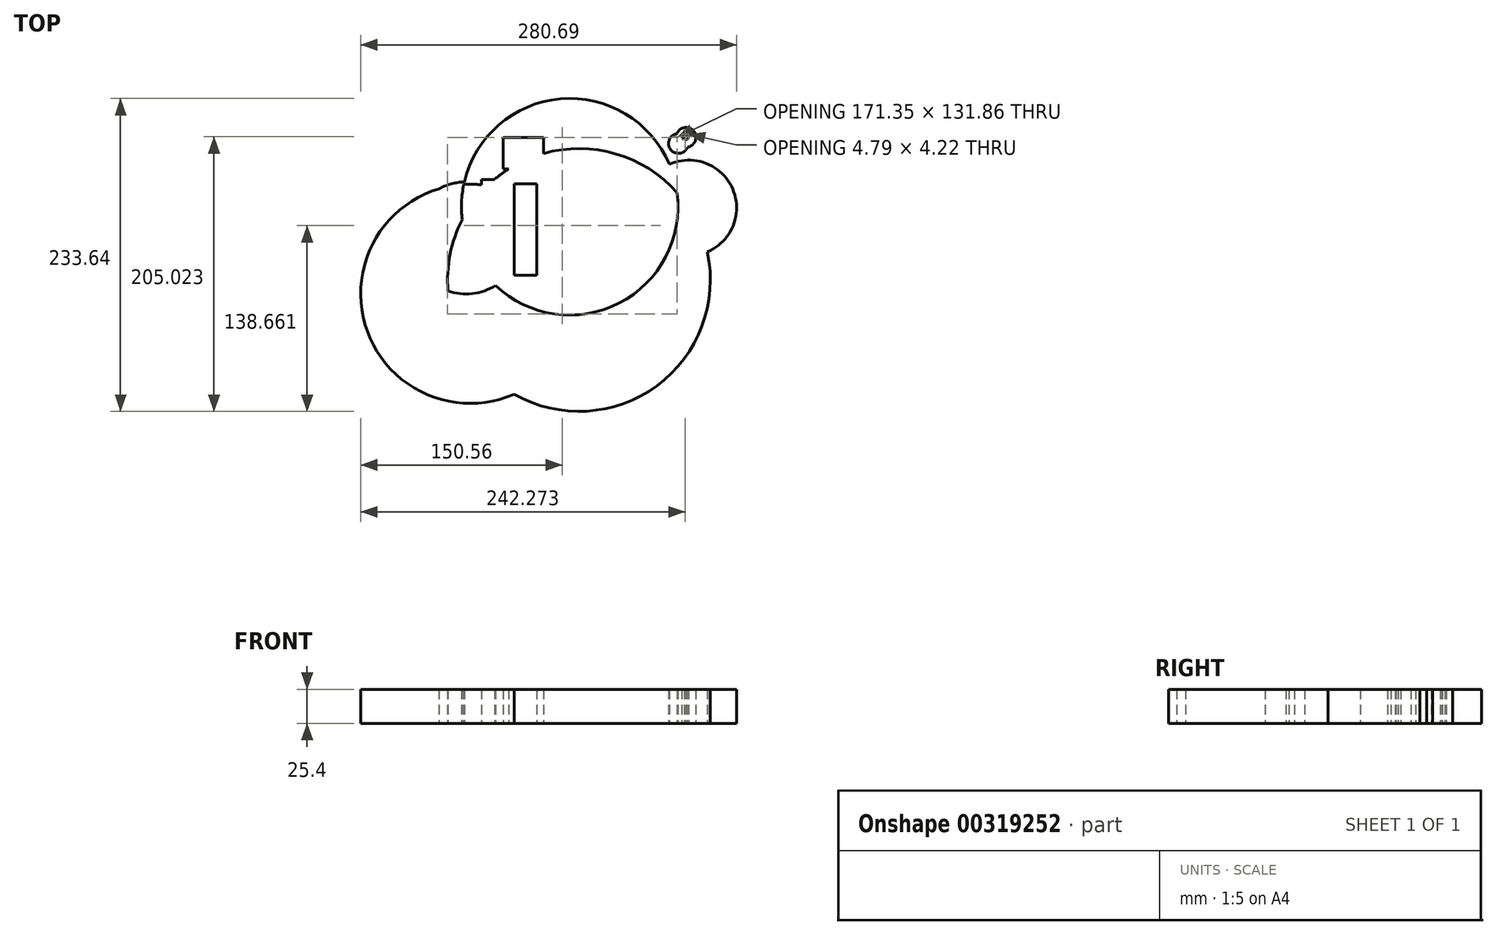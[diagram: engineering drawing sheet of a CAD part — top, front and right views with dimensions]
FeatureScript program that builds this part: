
annotation { "Feature Type Name" : "Feature", "Feature Type Description" : "" }
export const myFeature = defineFeature(function(context is Context, id is Id, definition is map)
    precondition{}
    {
        {
            var Q0;
            Q0=qCreatedBy(makeId("Top.planeOp"),FACE);
            var sketch = newSketch(context, id + "F0", { "sketchPlane" : qUnion([Q0])});
            skLineSegment(sketch, "E0.bottom", {"start": v(-49.5, 40.58) * mm, "end": v(-23.31, 40.58) * mm});
            skLineSegment(sketch, "E0.top", {"start": v(-49.5, -31.08) * mm, "end": v(-23.31, -31.08) * mm});
            skLineSegment(sketch, "E0.left", {"start": v(-49.5, 40.58) * mm, "end": v(-49.5, -31.08) * mm});
            skLineSegment(sketch, "E0.right", {"start": v(-23.31, 40.58) * mm, "end": v(-23.31, -31.08) * mm});
            skLineSegment(sketch, "E1.bottom", {"start": v(-33.39, 48.35) * mm, "end": v(-3.17, 48.35) * mm});
            skLineSegment(sketch, "E1.top", {"start": v(-33.39, 71.95) * mm, "end": v(-3.17, 71.95) * mm});
            skLineSegment(sketch, "E1.left", {"start": v(-33.39, 48.35) * mm, "end": v(-33.39, 71.95) * mm});
            skLineSegment(sketch, "E1.right", {"start": v(-3.17, 48.35) * mm, "end": v(-3.17, 71.95) * mm});
            skLineSegment(sketch, "E2", {"start": v(8.63, 35.11) * mm, "end": v(8.63, 6.04) * mm});
            skLineSegment(sketch, "E3", {"start": v(8.06, 6.04) * mm, "end": v(37.13, 6.04) * mm});
            skLineSegment(sketch, "E4", {"start": v(37.13, 6.04) * mm, "end": v(37.13, 35.11) * mm});
            skLineSegment(sketch, "E5", {"start": v(37.13, 35.11) * mm, "end": v(8.63, 35.11) * mm});
            skLineSegment(sketch, "E6", {"start": v(12.95, 44.03) * mm, "end": v(15.25, 63.32) * mm});
            skCircle(sketch, "E7", {"center": v(23.31, 21) * mm, "radius": 6.96 * mm});
            skCircle(sketch, "E8", {"center": v(16.4, 20.15) * mm, "radius": 80.85 * mm});
            skCircle(sketch, "E9", {"center": v(-61.01, -3.17) * mm, "radius": 41.85 * mm});
            skCircle(sketch, "E10", {"center": v(-57.85, -44.9) * mm, "radius": 81.82 * mm});
            skCircle(sketch, "E11", {"center": v(23.31, -34.54) * mm, "radius": 98.1 * mm});
            skCircle(sketch, "E12", {"center": v(105.34, 19.28) * mm, "radius": 35.68 * mm});
            skCircle(sketch, "E13", {"center": v(103.32, 71.95) * mm, "radius": 7.37 * mm});
            skCircle(sketch, "E14", {"center": v(97.57, 67.35) * mm, "radius": 7.37 * mm});
            skCircle(sketch, "E15", {"center": v(101.88, 72.81) * mm, "radius": 1.68 * mm});
            skCircle(sketch, "E16", {"center": v(103.32, 71.95) * mm, "radius": 1.68 * mm});
            skSolve(sketch);
        }
        {
            var Q0;
            Q0=qCreatedBy(makeId("Top.planeOp"),FACE);
            var sketch = newSketch(context, id + "F1", { "sketchPlane" : qUnion([Q0])});
            skLineSegment(sketch, "E17.bottom", {"start": v(-25.02, 37.34) * mm, "end": v(-8.17, 37.34) * mm});
            skLineSegment(sketch, "E17.top", {"start": v(-25.02, -30.94) * mm, "end": v(-8.17, -30.94) * mm});
            skLineSegment(sketch, "E17.left", {"start": v(-25.02, 37.34) * mm, "end": v(-25.02, -30.94) * mm});
            skLineSegment(sketch, "E17.right", {"start": v(-8.17, 37.34) * mm, "end": v(-8.17, -30.94) * mm});
            skSolve(sketch);
        }
        {
            var Q0;
            Q0 = qSketchRegion(id + "F0", true);
            var Q1;
            Q1 = qSketchRegion(id + "F1", true);
            extrude(context, id + "F2", {"entities" : qUnion([Q0, Q1]), "depth" : 25.4 * mm});
        }
    });
